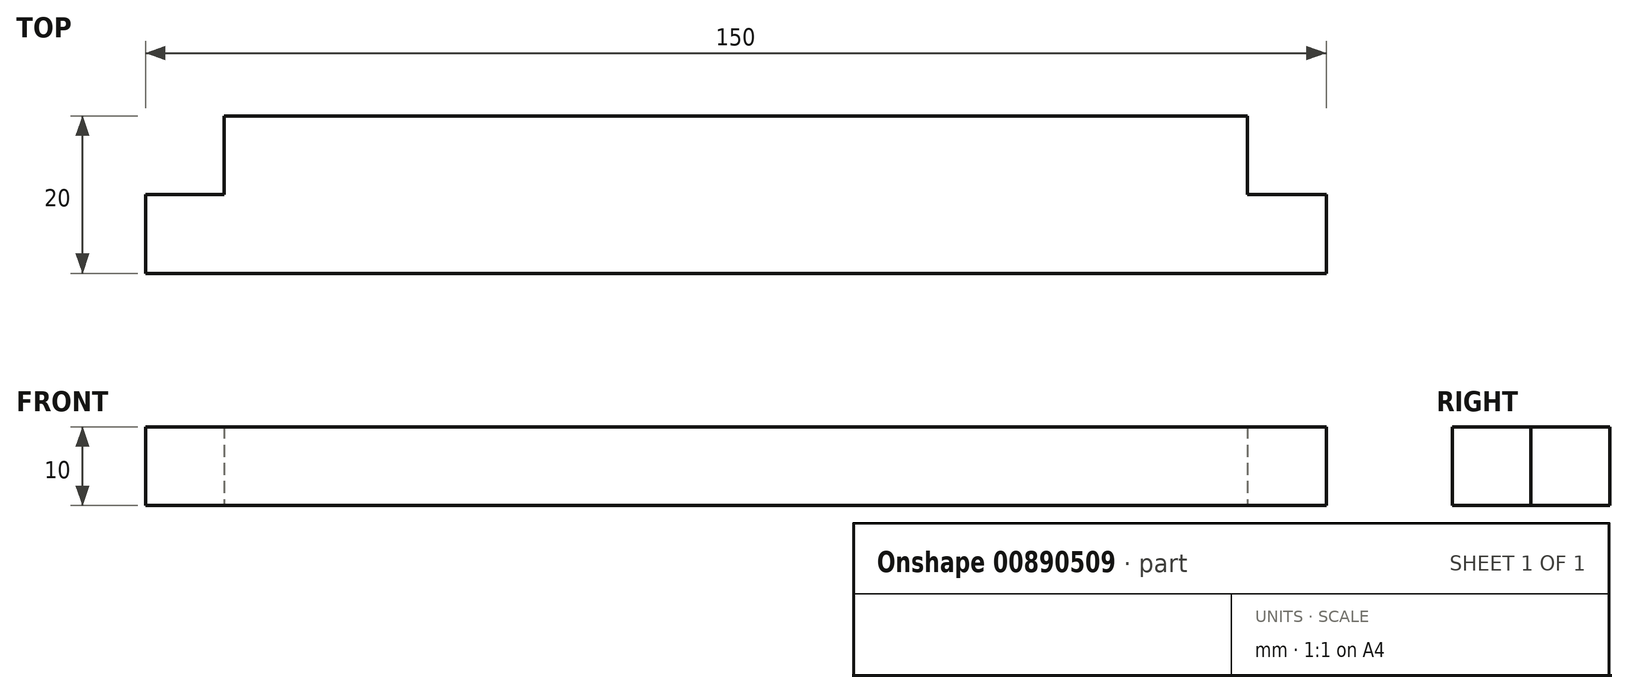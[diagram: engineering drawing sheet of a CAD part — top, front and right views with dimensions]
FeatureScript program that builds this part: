
annotation { "Feature Type Name" : "Feature", "Feature Type Description" : "" }
export const myFeature = defineFeature(function(context is Context, id is Id, definition is map)
    precondition{}
    {
        {
            var Q0;
            Q0=qCreatedBy(makeId("Top.planeOp"),FACE);
            var sketch = newSketch(context, id + "F0", { "sketchPlane" : qUnion([Q0])});
            skLineSegment(sketch, "E0.bottom", {"start": v(65, 10) * mm, "end": v(0, 10) * mm});
            skLineSegment(sketch, "E0.top", {"start": v(75, -10) * mm, "end": v(0, -10) * mm});
            skLineSegment(sketch, "E0.left", {"start": v(75, 0) * mm, "end": v(75, -10) * mm});
            skPoint(sketch, "E0.middle", {"position": v(0, 0) * mm});
            skLineSegment(sketch, "E1", {"start": v(75, 0) * mm, "end": v(65, 0) * mm});
            skLineSegment(sketch, "E2", {"start": v(65, 0) * mm, "end": v(65, 10) * mm});
            skPoint(sketch, "E0.right.start.orphan", {"position": v(-75, 10) * mm});
            skPoint(sketch, "E3.orphan", {"position": v(-75, -10) * mm});
            skLineSegment(sketch, "E4.MirrorCS", {"start": v(-75, 0) * mm, "end": v(-65, 0) * mm});
            skLineSegment(sketch, "E5.MirrorCS", {"start": v(-75, 0) * mm, "end": v(-75, -10) * mm});
            skLineSegment(sketch, "E6.MirrorCS", {"start": v(-65, 10) * mm, "end": v(0, 10) * mm});
            skLineSegment(sketch, "E7.MirrorCS", {"start": v(-75, -10) * mm, "end": v(0, -10) * mm});
            skLineSegment(sketch, "E8.MirrorCS", {"start": v(-65, 0) * mm, "end": v(-65, 10) * mm});
            skPoint(sketch, "E9.orphan", {"position": v(75, 10) * mm});
            skSolve(sketch);
        }
        {
            var Q0;
            Q0=makeQuery(id+"F0.imprint","IMPRINT",FACE,{"disambiguationData":[TD([[makeQuery(id+"F0.imprint","IMPRINT",EDGE,{"derivedFrom":sQuery(id+"F0.wireOp",EDGE,"E0.bottom")}),1.0]])]});
            extrude(context, id + "F1", {"entities" : qUnion([Q0]), "depth" : 10 * mm, "offsetDistance" : 25 * mm});
        }
    });
